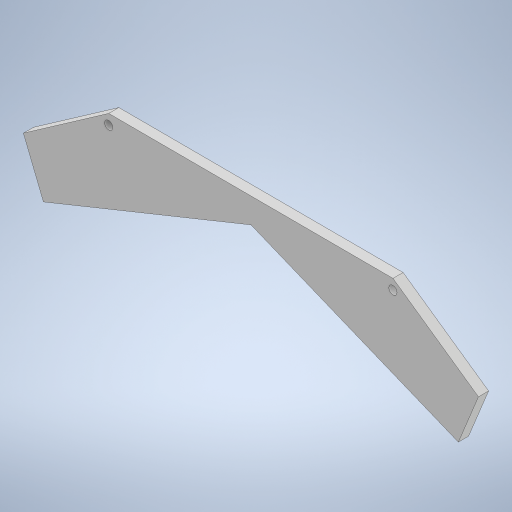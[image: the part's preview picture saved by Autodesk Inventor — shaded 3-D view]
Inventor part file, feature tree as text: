
AUTODESK INVENTOR PART (.ipt)
format: ipt  version: 2024 (Build 280153000, 153)  size: 263,680 bytes
history: native  units: mm
features: extrude x3, sketch x3, other x1
ambient origin geometry x8: Origin, YZ Plane, XZ Plane, XY Plane, X Axis, Y Axis, Z Axis, Center Point
bodies: Body1 (feature_tree)
feature tree (7):
  other  "Těleso1"
  extrude  "Vysunutí1"  Depth=140.0mm
  extrude  "Vysunutí2"  Depth=81.584mm
  extrude  "Vysunutí4"  Depth=6.108652mm
  sketch  "Náčrt1"
  sketch  "Náčrt2"
  sketch  "Náčrt5"
